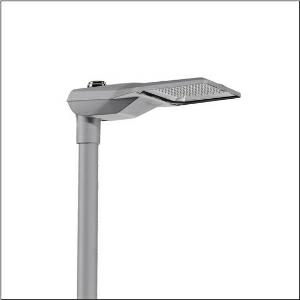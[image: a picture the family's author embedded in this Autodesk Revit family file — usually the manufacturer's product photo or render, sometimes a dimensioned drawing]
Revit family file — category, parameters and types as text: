
# Revit family: streetlight_sl_21_midi___stw1_0a_5xe7e37n08nb_3567
name_source: partatom
category: Lighting Fixtures
units: mm (PartAtom-declared; Revit-internal decimal feet)

## family parameters
Cut with Voids When Loaded = No
Host = Face
Light Source = No
Part Type = Normal
Room Calculation Point = No
Round Connector Dimension = Use Diameter
Shared = No

## types (1)
- --- (1 x LED, 22700 lm, 151.2 W, 3000K)
    Apparent Load = 151 VA
    CIE Flux Codes = 39 75 98 100 100
    Color Rendering = 70
    Color Temperature = 3000K
    Default Elevation = 1800 mm
    Description = Streetlight SL 21 midi, mast luminaire, primary light control with lens, of PMMA, primary optical cover: cover, of toughened safety glass, transparent, light distribution: STW1.0a, light emission: direct distribution, primary light characteristic: asymmetric, installation type: side-entry, LED, 3G 2.5mm², High Power LED, rated luminous flux: 22.700lm, luminous efficacy: 150lm/W, light colour: 730, colour temperature: 3000K, control gear: NEMA (7pin), control: overheat protection, pre-setting: linear dimming characteristic, constant luminous flux control, time-dependent luminous flux control, flexible luminous flux parameterisation, mains connection: 220..240V, AC, 50/60Hz, connection cable pre-assembled, cable length: 12,5m, wiring characteristics: H05VV-F, start of lifetime: 151W, end of service life: 157W, reduction: 70W, luminaire housing, of diecast aluminium (EN AC-44300), powder-coated, SITECO metallic grey (DB 702S), corrosivity category C5 high according to DIN EN ISO 12944, multi-level sealing system, sealing non-destructively replaceable, inclination adjustable: 0°, 5°, 10°, 15°, length: 644mm, width: 335mm, height: 110mm, spigot size: 42mm (side-entry), mounting height: 4..8m, protection rating (complete): IP66, insulation class (complete): insulation class I (protective earthing), certification: CE, ENEC, ENEC+, VDE, impact resistance: IK10, permissible operating ambient temperature for outdoor applications: -40..+50°C, standard-compliant lighting for roads and squares, packaging unit: 1 piece

Light Distribution: STW1.0a
    Height = 111 mm
    Lamp = 1 x LED
    Lamp Light Flux = 22700 lm
    Lamp Power = 151.2 W
    Lamp count = 1
    Length = 644 mm
    Luminous efficacy = 150 lm/W
    Manufacturer = Siteco
    ModVariant = No
    Model = 5XE7E37N08NB
    Number of Poles = 1
    OnlyDefault = Yes
    Power Factor = 1
    Product Name = Streetlight SL 21 midi | STW1.0a
    Product group = mast luminaire | pylon top
    ProductGroupID = 6100
    Protection Class = Protection class I
    Protection Degree = IP 66
    RLX_Detail_Level = 1
    RLX_Emergency_Light_Flux = 0 lm
    RLX_Emergency_Type = 0
    RLX_Emergency_Type_DB = No
    RlxData = <blob elided: 26661 chars, md5=ee11e881>
    Socket = socket
    Standby Power = 0 W
    System Light Flux = 22700 lm
    System Power = 151 W
    Type Comments = factory setting: luminous flux: 100 % | dim-lin: 254 | 802 mA
    Type Image = l_1294377.jpg
    URL = http://relux.com
    VarID = @adj_134429
    Voltage = 0 V
    Weight = 0.00 kg
    Width = 336 mm

## geometry (parser evidence)
native form markers: Blend x4, Sweep x10
no freeform markers — native parametric forms only
